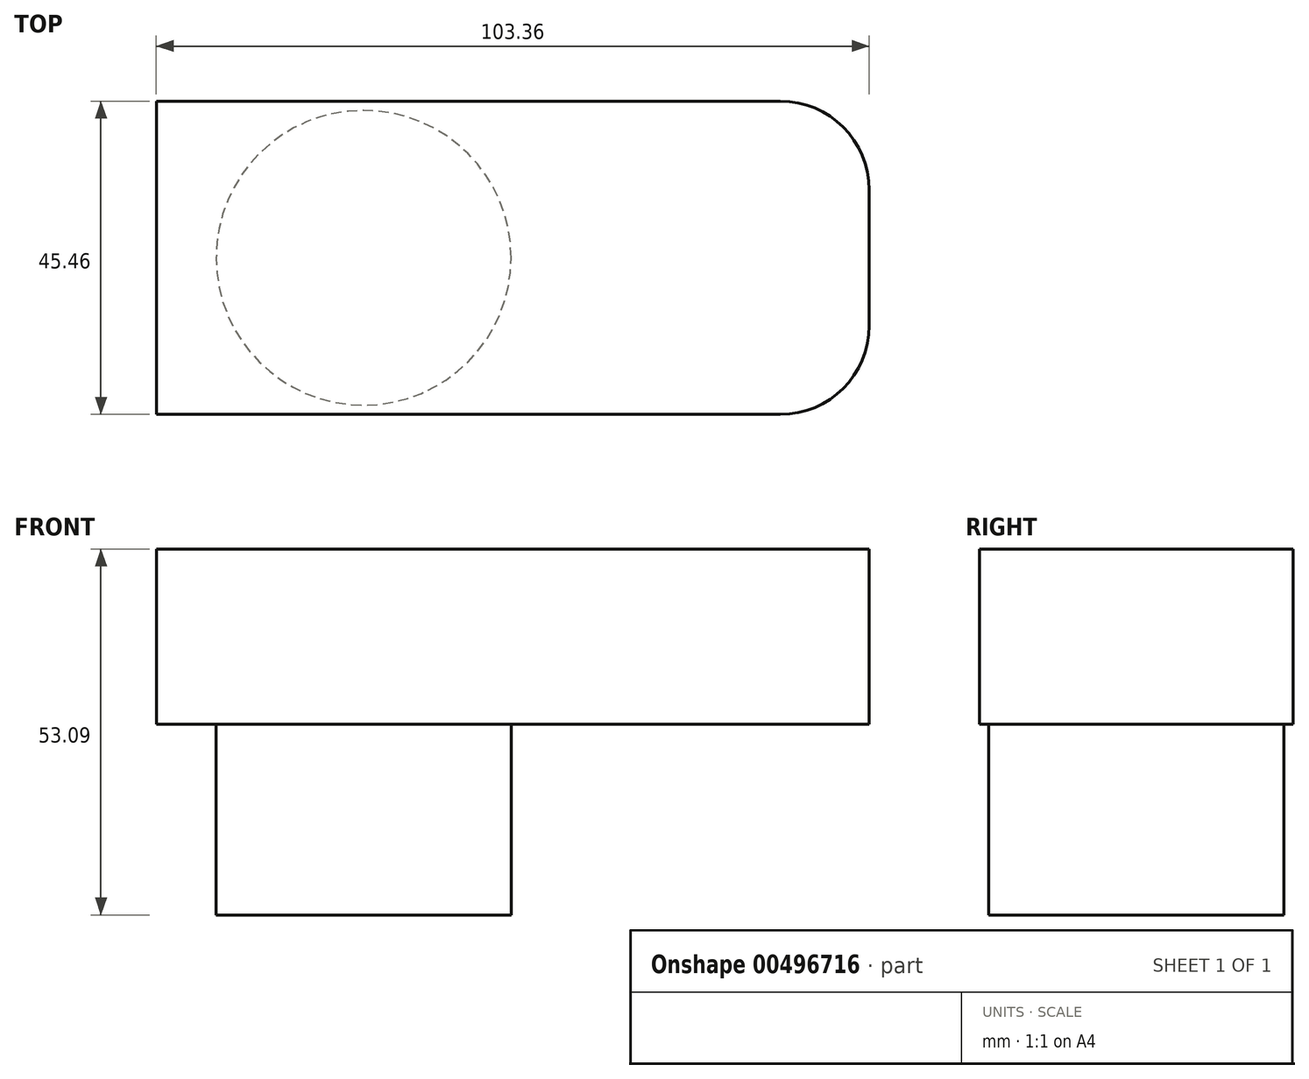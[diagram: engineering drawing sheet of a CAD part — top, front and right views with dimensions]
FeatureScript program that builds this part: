
annotation { "Feature Type Name" : "Feature", "Feature Type Description" : "" }
export const myFeature = defineFeature(function(context is Context, id is Id, definition is map)
    precondition{}
    {
        {
            var Q0;
            Q0=qCreatedBy(makeId("Top.planeOp"),FACE);
            var sketch = newSketch(context, id + "F0", { "sketchPlane" : qUnion([Q0])});
            skLineSegment(sketch, "E0.bottom", {"start": v(-51.68, 22.73) * mm, "end": v(51.68, 22.73) * mm});
            skLineSegment(sketch, "E0.top", {"start": v(-51.68, -22.73) * mm, "end": v(51.68, -22.73) * mm});
            skLineSegment(sketch, "E0.left", {"start": v(-51.68, 22.73) * mm, "end": v(-51.68, -22.73) * mm});
            skLineSegment(sketch, "E0.right", {"start": v(51.68, 22.73) * mm, "end": v(51.68, -22.73) * mm});
            skPoint(sketch, "E0.middle", {"position": v(0, 0) * mm});
            skSolve(sketch);
        }
        {
            var Q0;
            Q0 = qSketchRegion(id + "F0", true);
            var Q1;
            Q1=makeQuery(id+"F0.imprint","IMPRINT",FACE,{"disambiguationData":[TD([[makeQuery(id+"F0.imprint","IMPRINT",EDGE,{"derivedFrom":sQuery(id+"F0.wireOp",EDGE,"E0.bottom")}),-1.0]])]});
            extrude(context, id + "F1", {"entities" : qUnion([Q0, Q1]), "depth" : 25.4 * mm});
        }
        {
            var Q0;
            Q0=makeQuery(id+"F1.opExtrude","SWEPT_EDGE",EDGE,{"disambiguationData":[OSD([sQuery(id+"F0.wireOp",EDGE,"E0.bottom"),sQuery(id+"F0.wireOp",EDGE,"E0.right")])]});
            var Q1;
            Q1=makeQuery(id+"F1.opExtrude","SWEPT_EDGE",EDGE,{"disambiguationData":[OSD([sQuery(id+"F0.wireOp",EDGE,"E0.top"),sQuery(id+"F0.wireOp",EDGE,"E0.right")])]});
            fillet(context, id + "F2", {"entities" : qUnion([Q0, Q1]), "radius" : 12.88 * mm, "tangentPropagation" : true, "allowEdgeOverflow" : false});
        }
        {
            var Q0;
            Q0=qCreatedBy(makeId("Top.planeOp"),FACE);
            var sketch = newSketch(context, id + "F3", { "sketchPlane" : qUnion([Q0])});
            skCircle(sketch, "E1", {"center": v(-21.62, 0) * mm, "radius": 21.38 * mm});
            skSolve(sketch);
        }
        {
            var Q0;
            Q0=makeQuery(id+"F3.imprint","IMPRINT",FACE,{"disambiguationData":[TD([[makeQuery(id+"F3.imprint","IMPRINT",EDGE,{"derivedFrom":sQuery(id+"F3.wireOp",EDGE,"E1")}),1.0]])]});
            extrude(context, id + "F4", {"entities" : qUnion([Q0]), "operationType" : NewBodyOperationType.ADD, "oppositeDirection" : true, "depth" : 27.7 * mm});
        }
    });
